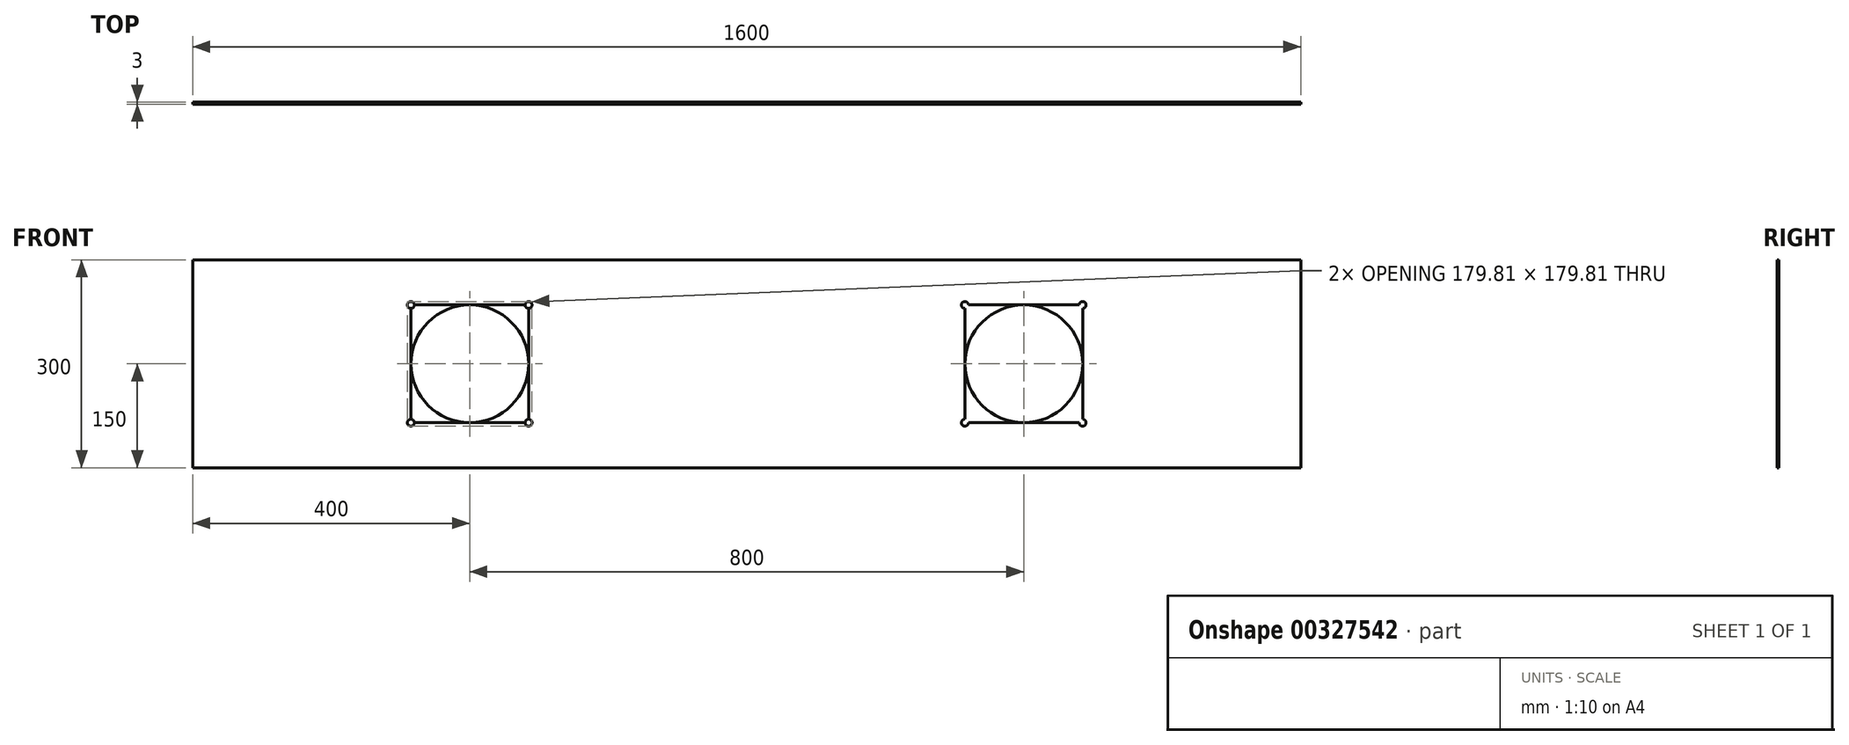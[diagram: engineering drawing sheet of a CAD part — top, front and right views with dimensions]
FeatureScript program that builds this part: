
annotation { "Feature Type Name" : "Feature", "Feature Type Description" : "" }
export const myFeature = defineFeature(function(context is Context, id is Id, definition is map)
    precondition{}
    {
        {
            var Q0;
            Q0=qCreatedBy(makeId("Front.planeOp"),FACE);
            var sketch = newSketch(context, id + "F0", { "sketchPlane" : qUnion([Q0])});
            skLineSegment(sketch, "E0.bottom", {"start": v(-800, 150) * mm, "end": v(800, 150) * mm});
            skLineSegment(sketch, "E0.top", {"start": v(-800, -150) * mm, "end": v(800, -150) * mm});
            skLineSegment(sketch, "E0.left", {"start": v(-800, 150) * mm, "end": v(-800, -150) * mm});
            skLineSegment(sketch, "E0.right", {"start": v(800, 150) * mm, "end": v(800, -150) * mm});
            skPoint(sketch, "E0.middle", {"position": v(0, 0) * mm});
            skCircle(sketch, "E1", {"center": v(-400, 0) * mm, "radius": 85 * mm});
            skCircle(sketch, "E2.MirrorC", {"center": v(400, 0) * mm, "radius": 85 * mm});
            skLineSegment(sketch, "E3.bottom", {"start": v(-315, 85) * mm, "end": v(-485, 85) * mm});
            skLineSegment(sketch, "E3.top", {"start": v(-315, -85) * mm, "end": v(-485, -85) * mm});
            skLineSegment(sketch, "E3.left", {"start": v(-315, 85) * mm, "end": v(-315, -85) * mm});
            skLineSegment(sketch, "E3.right", {"start": v(-485, 85) * mm, "end": v(-485, -85) * mm});
            skLineSegment(sketch, "E4.bottom", {"start": v(485, 85) * mm, "end": v(315, 85) * mm});
            skLineSegment(sketch, "E4.top", {"start": v(485, -85) * mm, "end": v(315, -85) * mm});
            skLineSegment(sketch, "E4.left", {"start": v(485, 85) * mm, "end": v(485, -85) * mm});
            skLineSegment(sketch, "E4.right", {"start": v(315, 85) * mm, "end": v(315, -85) * mm});
            skCircle(sketch, "E5", {"center": v(-485, 85) * mm, "radius": 5 * mm});
            skCircle(sketch, "E6", {"center": v(-315, 85) * mm, "radius": 5 * mm});
            skCircle(sketch, "E7", {"center": v(-485, -85) * mm, "radius": 5 * mm});
            skCircle(sketch, "E8", {"center": v(-315, -85) * mm, "radius": 5 * mm});
            skCircle(sketch, "E9", {"center": v(315, 85) * mm, "radius": 5 * mm});
            skCircle(sketch, "E10", {"center": v(485, 85) * mm, "radius": 5 * mm});
            skCircle(sketch, "E11", {"center": v(315, -85) * mm, "radius": 5 * mm});
            skCircle(sketch, "E12", {"center": v(485, -85) * mm, "radius": 5 * mm});
            skSolve(sketch);
        }
        {
            var Q0;
            Q0=makeQuery(id+"F0.imprint","IMPRINT",FACE,{"disambiguationData":[TD([[makeQuery(id+"F0.imprint","IMPRINT",EDGE,{"derivedFrom":sQuery(id+"F0.wireOp",EDGE,"E0.bottom")}),-1.0]])]});
            var Q1;
            {var subQ0=sQuery(id+"F0.wireOp",EDGE,"E3.bottom");var subQ1=sQuery(id+"F0.wireOp",EDGE,"E1");var subQ2=makeQuery(id+"F0.imprint","INTERSECT",VERTEX,{"derivedFrom":[subQ1,subQ0]});Q1=makeQuery(id+"F0.imprint","IMPRINT",FACE,{"disambiguationData":[TD([[makeQuery(id+"F0.imprint","IMPRINT",EDGE,{"disambiguationData":[TD([[subQ2,-1.0]])],"derivedFrom":subQ1}),-1.0]])]});}
            var Q2;
            {var subQ0=sQuery(id+"F0.wireOp",EDGE,"E3.bottom");var subQ1=sQuery(id+"F0.wireOp",EDGE,"E1");var subQ2=makeQuery(id+"F0.imprint","INTERSECT",VERTEX,{"derivedFrom":[subQ1,subQ0]});Q2=makeQuery(id+"F0.imprint","IMPRINT",FACE,{"disambiguationData":[TD([[makeQuery(id+"F0.imprint","IMPRINT",EDGE,{"disambiguationData":[TD([[subQ2,1.0]])],"derivedFrom":subQ1}),-1.0]])]});}
            var Q3;
            {var subQ0=sQuery(id+"F0.wireOp",EDGE,"E3.right");var subQ1=sQuery(id+"F0.wireOp",EDGE,"E1");var subQ2=makeQuery(id+"F0.imprint","INTERSECT",VERTEX,{"derivedFrom":[subQ1,subQ0]});Q3=makeQuery(id+"F0.imprint","IMPRINT",FACE,{"disambiguationData":[TD([[makeQuery(id+"F0.imprint","IMPRINT",EDGE,{"disambiguationData":[TD([[subQ2,-1.0]])],"derivedFrom":subQ1}),-1.0]])]});}
            var Q4;
            {var subQ0=sQuery(id+"F0.wireOp",EDGE,"E3.left");var subQ1=sQuery(id+"F0.wireOp",EDGE,"E1");var subQ2=makeQuery(id+"F0.imprint","INTERSECT",VERTEX,{"derivedFrom":[subQ1,subQ0]});Q4=makeQuery(id+"F0.imprint","IMPRINT",FACE,{"disambiguationData":[TD([[makeQuery(id+"F0.imprint","IMPRINT",EDGE,{"disambiguationData":[TD([[subQ2,1.0]])],"derivedFrom":subQ1}),-1.0]])]});}
            var Q5;
            {var subQ0=sQuery(id+"F0.wireOp",EDGE,"E4.bottom");var subQ1=sQuery(id+"F0.wireOp",EDGE,"E2.MirrorC");var subQ2=makeQuery(id+"F0.imprint","INTERSECT",VERTEX,{"derivedFrom":[subQ1,subQ0]});Q5=makeQuery(id+"F0.imprint","IMPRINT",FACE,{"disambiguationData":[TD([[makeQuery(id+"F0.imprint","IMPRINT",EDGE,{"disambiguationData":[TD([[subQ2,1.0]])],"derivedFrom":subQ1}),1.0]])]});}
            var Q6;
            {var subQ0=sQuery(id+"F0.wireOp",EDGE,"E4.bottom");var subQ1=sQuery(id+"F0.wireOp",EDGE,"E2.MirrorC");var subQ2=makeQuery(id+"F0.imprint","INTERSECT",VERTEX,{"derivedFrom":[subQ1,subQ0]});Q6=makeQuery(id+"F0.imprint","IMPRINT",FACE,{"disambiguationData":[TD([[makeQuery(id+"F0.imprint","IMPRINT",EDGE,{"disambiguationData":[TD([[subQ2,-1.0]])],"derivedFrom":subQ1}),1.0]])]});}
            var Q7;
            {var subQ0=sQuery(id+"F0.wireOp",EDGE,"E4.right");var subQ1=sQuery(id+"F0.wireOp",EDGE,"E2.MirrorC");var subQ2=makeQuery(id+"F0.imprint","INTERSECT",VERTEX,{"derivedFrom":[subQ1,subQ0]});Q7=makeQuery(id+"F0.imprint","IMPRINT",FACE,{"disambiguationData":[TD([[makeQuery(id+"F0.imprint","IMPRINT",EDGE,{"disambiguationData":[TD([[subQ2,1.0]])],"derivedFrom":subQ1}),1.0]])]});}
            var Q8;
            {var subQ0=sQuery(id+"F0.wireOp",EDGE,"E4.left");var subQ1=sQuery(id+"F0.wireOp",EDGE,"E2.MirrorC");var subQ2=makeQuery(id+"F0.imprint","INTERSECT",VERTEX,{"derivedFrom":[subQ1,subQ0]});Q8=makeQuery(id+"F0.imprint","IMPRINT",FACE,{"disambiguationData":[TD([[makeQuery(id+"F0.imprint","IMPRINT",EDGE,{"disambiguationData":[TD([[subQ2,-1.0]])],"derivedFrom":subQ1}),1.0]])]});}
            extrude(context, id + "F1", {"entities" : qUnion([Q0, Q1, Q2, Q3, Q4, Q5, Q6, Q7, Q8]), "depth" : 3 * mm, "symmetric" : true});
        }
    });
